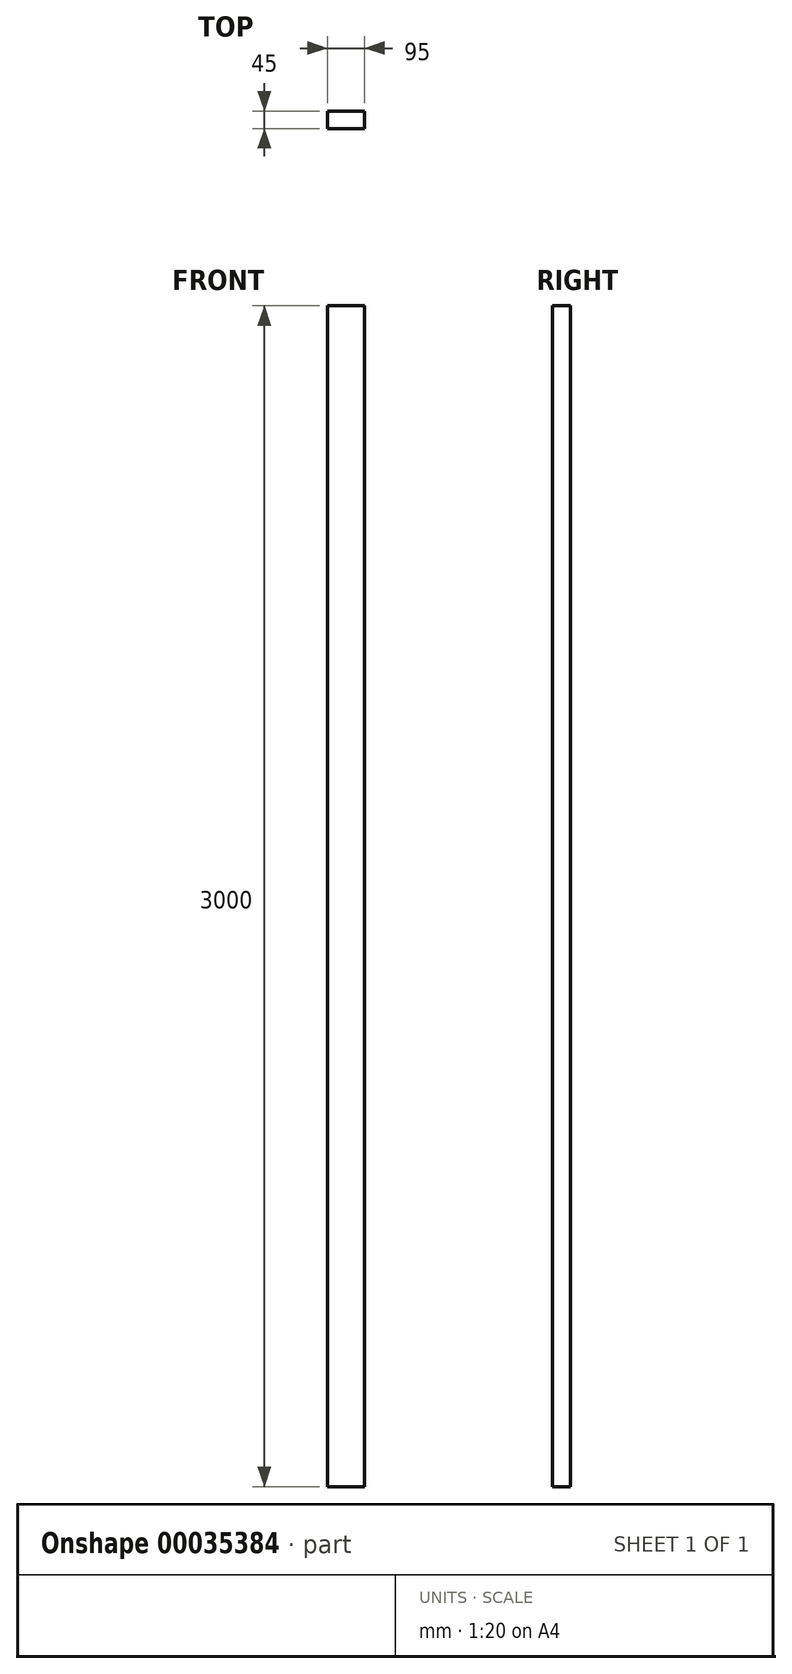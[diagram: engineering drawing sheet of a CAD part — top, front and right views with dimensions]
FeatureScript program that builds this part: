
annotation { "Feature Type Name" : "Feature", "Feature Type Description" : "" }
export const myFeature = defineFeature(function(context is Context, id is Id, definition is map)
    precondition{}
    {
        {
            var Q0;
            Q0=qCreatedBy(makeId("Top.planeOp"),FACE);
            var sketch = newSketch(context, id + "F0", { "sketchPlane" : qUnion([Q0])});
            skLineSegment(sketch, "E0.rect.bottom", {"start": v(47.5, -22.5) * mm, "end": v(-47.5, -22.5) * mm});
            skLineSegment(sketch, "E0.rect.top", {"start": v(47.5, 22.5) * mm, "end": v(-47.5, 22.5) * mm});
            skLineSegment(sketch, "E0.rect.left", {"start": v(47.5, -22.5) * mm, "end": v(47.5, 22.5) * mm});
            skLineSegment(sketch, "E0.rect.right", {"start": v(-47.5, -22.5) * mm, "end": v(-47.5, 22.5) * mm});
            skPoint(sketch, "E0.rect.middle", {"position": v(0, 0) * mm});
            skSolve(sketch);
        }
        {
            var Q0;
            Q0=makeQuery(id+"F0.imprint","IMPRINT",FACE,{"disambiguationData":[TD([[makeQuery(id+"F0.imprint","IMPRINT",EDGE,{"derivedFrom":sQuery(id+"F0.wireOp",EDGE,"E0.rect.bottom")}),-1.0]])]});
            extrude(context, id + "F1", {"entities" : qUnion([Q0]), "depth" : 3000 * mm});
        }
    });
